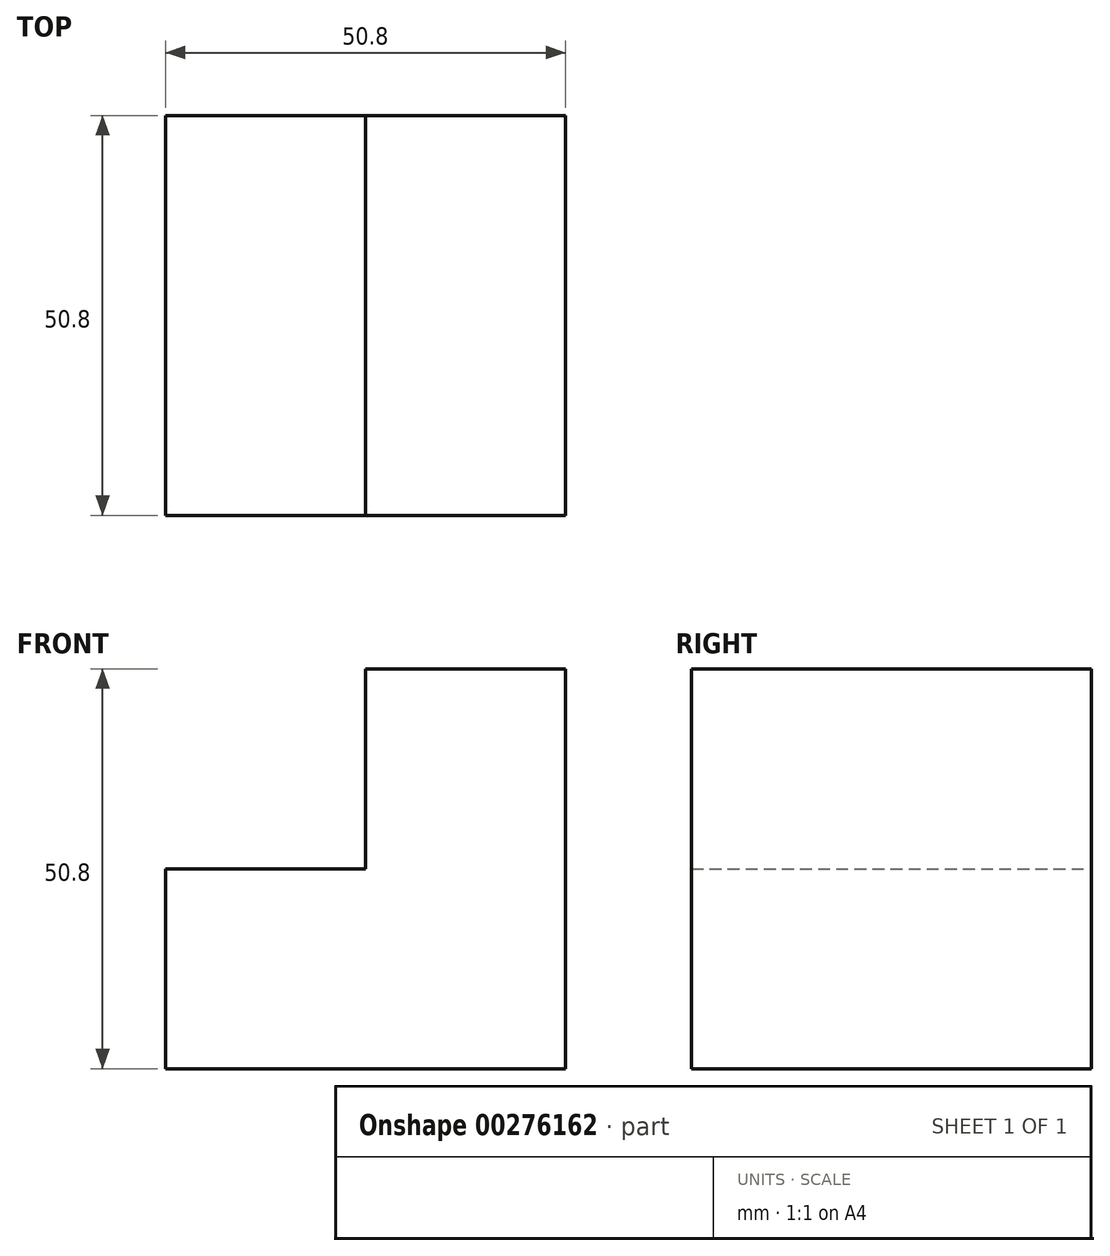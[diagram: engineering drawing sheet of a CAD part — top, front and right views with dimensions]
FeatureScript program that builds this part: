
annotation { "Feature Type Name" : "Feature", "Feature Type Description" : "" }
export const myFeature = defineFeature(function(context is Context, id is Id, definition is map)
    precondition{}
    {
        {
            var Q0;
            Q0=qCreatedBy(makeId("Front.planeOp"),FACE);
            var sketch = newSketch(context, id + "F0", { "sketchPlane" : qUnion([Q0])});
            skLineSegment(sketch, "E0", {"start": v(0, 0) * mm, "end": v(-50.8, 0) * mm});
            skLineSegment(sketch, "E1", {"start": v(-50.8, 0) * mm, "end": v(-50.8, 25.4) * mm});
            skLineSegment(sketch, "E2", {"start": v(-50.8, 25.4) * mm, "end": v(-25.4, 25.4) * mm});
            skLineSegment(sketch, "E3", {"start": v(-25.4, 25.4) * mm, "end": v(-25.4, 50.8) * mm});
            skLineSegment(sketch, "E4", {"start": v(-25.4, 50.8) * mm, "end": v(0, 50.8) * mm});
            skLineSegment(sketch, "E5", {"start": v(0, 50.8) * mm, "end": v(0, 0) * mm});
            skSolve(sketch);
        }
        {
            var Q0;
            Q0 = qSketchRegion(id + "F0", true);
            extrude(context, id + "F1", {"entities" : qUnion([Q0]), "depth" : 50.8 * mm});
        }
    });
